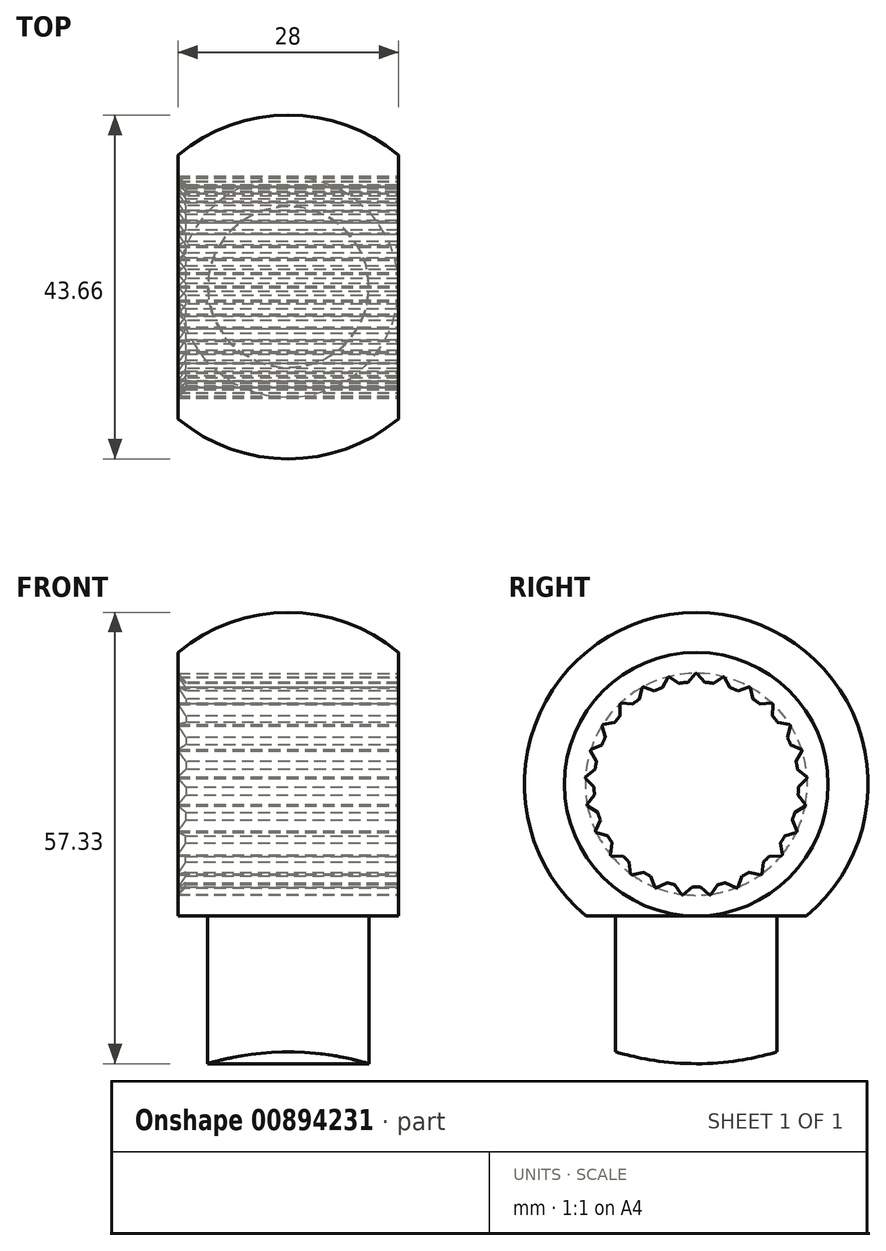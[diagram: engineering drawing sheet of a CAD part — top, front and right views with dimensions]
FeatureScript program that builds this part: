
annotation { "Feature Type Name" : "Feature", "Feature Type Description" : "" }
export const myFeature = defineFeature(function(context is Context, id is Id, definition is map)
    precondition{}
    {
        {
            var Q0;
            Q0=qCreatedBy(makeId("Front.planeOp"),FACE);
            var sketch = newSketch(context, id + "F0", { "sketchPlane" : qUnion([Q0])});
            skLineSegment(sketch, "E0", {"start": v(1, 13) * mm, "end": v(28, 13) * mm});
            skLineSegment(sketch, "E1", {"start": v(1, 13) * mm, "end": v(0, 14.1) * mm});
            skLineSegment(sketch, "E2", {"start": v(0, 14.1) * mm, "end": v(0, 16.75) * mm});
            skArc(sketch, "E3", {"start": v(28, 16.75) * mm, "mid": v(14, 21.83) * mm, "end": v(0, 16.75) * mm});
            skLineSegment(sketch, "E4", {"start": v(28, 16.75) * mm, "end": v(28, 13) * mm});
            skLineSegment(sketch, "E5", {"start": v(0, 0) * mm, "end": v(28, 0) * mm, "construction": true});
            skSolve(sketch);
        }
        {
            var Q0;
            Q0=makeQuery(id+"F0.imprint","IMPRINT",FACE,{"disambiguationData":[TD([[makeQuery(id+"F0.imprint","IMPRINT",EDGE,{"derivedFrom":sQuery(id+"F0.wireOp",EDGE,"E0")}),1.0]])]});
            var Q1;
            Q1=sQuery(id+"F0.wireOp",EDGE,"E5");
            revolve(context, id + "F1", {"surfaceOperationType" : NewSurfaceOperationType.NEW, "entities" : qUnion([Q0]), "axis" : qUnion([Q1]), "revolveType" : RevolveType.FULL});
        }
        {
            var Q0;
            Q0=qCreatedBy(makeId("Top.planeOp"),FACE);
            var sketch = newSketch(context, id + "F2", { "sketchPlane" : qUnion([Q0])});
            skCircle(sketch, "E6", {"center": v(14, 0) * mm, "radius": 10.25 * mm});
            skCircle(sketch, "E7", {"center": v(14, 0) * mm, "radius": 14 * mm});
            skSolve(sketch);
        }
        {
            var Q0;
            Q0=makeQuery(id+"F2.imprint","IMPRINT",FACE,{"disambiguationData":[TD([[makeQuery(id+"F2.imprint","IMPRINT",EDGE,{"derivedFrom":sQuery(id+"F2.wireOp",EDGE,"E6")}),-1.0]])]});
            extrude(context, id + "F3", {"entities" : qUnion([Q0]), "operationType" : NewBodyOperationType.REMOVE, "oppositeDirection" : true, "depth" : 21 * mm, "offsetDistance" : 25 * mm, "hasSecondDirection" : true, "secondDirectionOppositeDirection" : true, "secondDirectionDepth" : 16.75 * mm});
        }
        {
            var Q0;
            Q0=makeQuery(id+"F3.boolean.opBoolean","COPY",FACE,{"derivedFrom":makeQuery(id+"F3.opExtrude","CAP_FACE",FACE,{"disambiguationData":[OSD([sQuery(id+"F2.wireOp",EDGE,"E6"),sQuery(id+"F2.wireOp",EDGE,"E7")])],"isStart":true})});
            var sketch = newSketch(context, id + "F4", { "sketchPlane" : qUnion([Q0])});
            skCircle(sketch, "E8.0", {"center": v(14, 0) * mm, "radius": 10.25 * mm});
            skSolve(sketch);
        }
        {
            var Q0;
            Q0=qSketchRegion(id+"F4",true);
            extrude(context, id + "F5", {"entities" : qUnion([Q0]), "operationType" : NewBodyOperationType.ADD, "depth" : 20 * mm, "offsetDistance" : 25 * mm});
        }
        {
            var Q0;
            Q0=makeQuery(id+"F1.opRevolve","SWEPT_FACE",FACE,{"disambiguationData":[OSD([sQuery(id+"F0.wireOp",EDGE,"E2")])]});
            var sketch = newSketch(context, id + "F6", { "sketchPlane" : qUnion([Q0])});
            skCircle(sketch, "E9", {"center": v(0, 0) * mm, "radius": 35.5 * mm});
            skCircle(sketch, "E10", {"center": v(0, 0) * mm, "radius": 40 * mm});
            skSolve(sketch);
        }
        {
            var Q0;
            Q0=makeQuery(id+"F6.imprint","IMPRINT",FACE,{"disambiguationData":[TD([[makeQuery(id+"F6.imprint","IMPRINT",EDGE,{"derivedFrom":sQuery(id+"F6.wireOp",EDGE,"E9")}),-1.0]])]});
            extrude(context, id + "F7", {"entities" : qUnion([Q0]), "operationType" : NewBodyOperationType.REMOVE, "endBound" : BoundingType.THROUGH_ALL, "oppositeDirection" : true, "depth" : 25 * mm, "offsetDistance" : 25 * mm});
        }
        {
            var Q0;
            Q0=makeQuery(id+"F1.opRevolve","SWEPT_FACE",FACE,{"disambiguationData":[OSD([sQuery(id+"F0.wireOp",EDGE,"E4")])]});
            var sketch = newSketch(context, id + "F8", { "sketchPlane" : qUnion([Q0])});
            skArc(sketch, "E11", {"start": v(1.63, 12.85) * mm, "mid": v(1.38, 12.88) * mm, "end": v(1.13, 12.9) * mm});
            skArc(sketch, "E12", {"start": v(0.1, 14.05) * mm, "mid": v(0.05, 14.05) * mm, "end": v(0, 14.05) * mm});
            skLineSegment(sketch, "E13", {"start": v(0.1, 14.05) * mm, "end": v(1.13, 12.9) * mm});
            skArc(sketch, "E14", {"start": v(-1.13, 12.9) * mm, "mid": v(-1.38, 12.88) * mm, "end": v(-1.63, 12.85) * mm});
            skArc(sketch, "E15", {"start": v(0, 14.05) * mm, "mid": v(-0.05, 14.05) * mm, "end": v(-0.1, 14.05) * mm});
            skLineSegment(sketch, "E16", {"start": v(-0.1, 14.05) * mm, "end": v(-1.13, 12.9) * mm});
            skArc(sketch, "E17", {"start": v(-1.63, 12.85) * mm, "mid": v(-1.88, 12.81) * mm, "end": v(-2.13, 12.78) * mm});
            skArc(sketch, "E18", {"start": v(-3.4, 13.63) * mm, "mid": v(-3.46, 13.62) * mm, "end": v(-3.5, 13.6) * mm});
            skLineSegment(sketch, "E19", {"start": v(-3.4, 13.63) * mm, "end": v(-2.13, 12.78) * mm});
            skArc(sketch, "E20", {"start": v(-4.31, 12.21) * mm, "mid": v(-4.55, 12.13) * mm, "end": v(-4.79, 12.04) * mm});
            skArc(sketch, "E21", {"start": v(-3.5, 13.6) * mm, "mid": v(-3.55, 13.6) * mm, "end": v(-3.6, 13.58) * mm});
            skLineSegment(sketch, "E22", {"start": v(-3.6, 13.58) * mm, "end": v(-4.31, 12.21) * mm});
            skArc(sketch, "E23", {"start": v(-4.79, 12.04) * mm, "mid": v(-5.02, 11.94) * mm, "end": v(-5.25, 11.84) * mm});
            skArc(sketch, "E24", {"start": v(-6.7, 12.35) * mm, "mid": v(-6.75, 12.33) * mm, "end": v(-6.8, 12.3) * mm});
            skLineSegment(sketch, "E25", {"start": v(-6.7, 12.35) * mm, "end": v(-5.25, 11.84) * mm});
            skArc(sketch, "E26", {"start": v(-7.23, 10.76) * mm, "mid": v(-7.44, 10.61) * mm, "end": v(-7.64, 10.47) * mm});
            skArc(sketch, "E27", {"start": v(-6.8, 12.3) * mm, "mid": v(-6.84, 12.28) * mm, "end": v(-6.88, 12.26) * mm});
            skLineSegment(sketch, "E28", {"start": v(-6.88, 12.26) * mm, "end": v(-7.23, 10.76) * mm});
            skArc(sketch, "E29", {"start": v(-7.64, 10.47) * mm, "mid": v(-7.84, 10.32) * mm, "end": v(-8.04, 10.16) * mm});
            skArc(sketch, "E30", {"start": v(-9.58, 10.3) * mm, "mid": v(-9.62, 10.26) * mm, "end": v(-9.65, 10.23) * mm});
            skLineSegment(sketch, "E31", {"start": v(-9.58, 10.3) * mm, "end": v(-8.04, 10.16) * mm});
            skArc(sketch, "E32", {"start": v(-9.69, 8.62) * mm, "mid": v(-9.85, 8.43) * mm, "end": v(-10.02, 8.24) * mm});
            skArc(sketch, "E33", {"start": v(-9.65, 10.23) * mm, "mid": v(-9.69, 10.2) * mm, "end": v(-9.72, 10.16) * mm});
            skLineSegment(sketch, "E34", {"start": v(-9.72, 10.16) * mm, "end": v(-9.69, 8.62) * mm});
            skArc(sketch, "E35", {"start": v(-10.02, 8.24) * mm, "mid": v(-10.18, 8.04) * mm, "end": v(-10.33, 7.84) * mm});
            skArc(sketch, "E36", {"start": v(-11.85, 7.59) * mm, "mid": v(-11.88, 7.55) * mm, "end": v(-11.9, 7.5) * mm});
            skLineSegment(sketch, "E37", {"start": v(-11.85, 7.59) * mm, "end": v(-10.33, 7.84) * mm});
            skArc(sketch, "E38", {"start": v(-11.54, 5.94) * mm, "mid": v(-11.65, 5.71) * mm, "end": v(-11.76, 5.49) * mm});
            skArc(sketch, "E39", {"start": v(-11.9, 7.5) * mm, "mid": v(-11.93, 7.46) * mm, "end": v(-11.96, 7.42) * mm});
            skLineSegment(sketch, "E40", {"start": v(-11.96, 7.42) * mm, "end": v(-11.54, 5.94) * mm});
            skArc(sketch, "E41", {"start": v(-11.76, 5.49) * mm, "mid": v(-11.87, 5.26) * mm, "end": v(-11.97, 5.03) * mm});
            skArc(sketch, "E42", {"start": v(-13.38, 4.4) * mm, "mid": v(-13.4, 4.36) * mm, "end": v(-13.4, 4.3) * mm});
            skLineSegment(sketch, "E43", {"start": v(-13.38, 4.4) * mm, "end": v(-11.97, 5.03) * mm});
            skArc(sketch, "E44", {"start": v(-12.67, 2.88) * mm, "mid": v(-12.72, 2.63) * mm, "end": v(-12.77, 2.39) * mm});
            skArc(sketch, "E45", {"start": v(-13.4, 4.3) * mm, "mid": v(-13.43, 4.26) * mm, "end": v(-13.44, 4.21) * mm});
            skLineSegment(sketch, "E46", {"start": v(-13.44, 4.21) * mm, "end": v(-12.67, 2.88) * mm});
            skArc(sketch, "E47", {"start": v(-12.77, 2.39) * mm, "mid": v(-12.81, 2.14) * mm, "end": v(-12.85, 1.89) * mm});
            skArc(sketch, "E48", {"start": v(-14.07, 0.94) * mm, "mid": v(-14.07, 0.89) * mm, "end": v(-14.07, 0.84) * mm});
            skLineSegment(sketch, "E49", {"start": v(-14.07, 0.94) * mm, "end": v(-12.85, 1.89) * mm});
            skArc(sketch, "E50", {"start": v(-13, -0.36) * mm, "mid": v(-12.99, -0.61) * mm, "end": v(-12.97, -0.87) * mm});
            skArc(sketch, "E51", {"start": v(-14.07, 0.84) * mm, "mid": v(-14.08, 0.79) * mm, "end": v(-14.08, 0.74) * mm});
            skLineSegment(sketch, "E52", {"start": v(-14.08, 0.74) * mm, "end": v(-13, -0.36) * mm});
            skArc(sketch, "E53", {"start": v(-12.97, -0.87) * mm, "mid": v(-12.96, -1.12) * mm, "end": v(-12.93, -1.37) * mm});
            skArc(sketch, "E54", {"start": v(-13.87, -2.6) * mm, "mid": v(-13.86, -2.64) * mm, "end": v(-13.85, -2.7) * mm});
            skLineSegment(sketch, "E55", {"start": v(-13.87, -2.6) * mm, "end": v(-12.93, -1.37) * mm});
            skArc(sketch, "E56", {"start": v(-12.51, -3.58) * mm, "mid": v(-12.44, -3.83) * mm, "end": v(-12.36, -4.07) * mm});
            skArc(sketch, "E57", {"start": v(-13.85, -2.7) * mm, "mid": v(-13.84, -2.74) * mm, "end": v(-13.83, -2.79) * mm});
            skLineSegment(sketch, "E58", {"start": v(-13.83, -2.79) * mm, "end": v(-12.51, -3.58) * mm});
            skArc(sketch, "E59", {"start": v(-12.36, -4.07) * mm, "mid": v(-12.28, -4.3) * mm, "end": v(-12.2, -4.54) * mm});
            skArc(sketch, "E60", {"start": v(-12.8, -5.96) * mm, "mid": v(-12.78, -6) * mm, "end": v(-12.76, -6.05) * mm});
            skLineSegment(sketch, "E61", {"start": v(-12.8, -5.96) * mm, "end": v(-12.2, -4.54) * mm});
            skArc(sketch, "E62", {"start": v(-11.24, -6.58) * mm, "mid": v(-11.1, -6.8) * mm, "end": v(-10.98, -7.02) * mm});
            skArc(sketch, "E63", {"start": v(-12.76, -6.05) * mm, "mid": v(-12.74, -6.1) * mm, "end": v(-12.72, -6.14) * mm});
            skLineSegment(sketch, "E64", {"start": v(-12.72, -6.14) * mm, "end": v(-11.24, -6.58) * mm});
            skArc(sketch, "E65", {"start": v(-10.98, -7.02) * mm, "mid": v(-10.84, -7.23) * mm, "end": v(-10.7, -7.44) * mm});
            skArc(sketch, "E66", {"start": v(-10.93, -8.96) * mm, "mid": v(-10.9, -9) * mm, "end": v(-10.86, -9.04) * mm});
            skLineSegment(sketch, "E67", {"start": v(-10.93, -8.96) * mm, "end": v(-10.7, -7.44) * mm});
            skArc(sketch, "E68", {"start": v(-9.26, -9.17) * mm, "mid": v(-9.08, -9.35) * mm, "end": v(-8.9, -9.53) * mm});
            skArc(sketch, "E69", {"start": v(-10.86, -9.04) * mm, "mid": v(-10.83, -9.08) * mm, "end": v(-10.8, -9.11) * mm});
            skLineSegment(sketch, "E70", {"start": v(-10.8, -9.11) * mm, "end": v(-9.26, -9.17) * mm});
            skArc(sketch, "E71", {"start": v(-8.9, -9.53) * mm, "mid": v(-8.71, -9.7) * mm, "end": v(-8.53, -9.86) * mm});
            skArc(sketch, "E72", {"start": v(-8.37, -11.4) * mm, "mid": v(-8.33, -11.43) * mm, "end": v(-8.29, -11.46) * mm});
            skLineSegment(sketch, "E73", {"start": v(-8.37, -11.4) * mm, "end": v(-8.53, -9.86) * mm});
            skArc(sketch, "E74", {"start": v(-6.7, -11.2) * mm, "mid": v(-6.48, -11.32) * mm, "end": v(-6.26, -11.44) * mm});
            skArc(sketch, "E75", {"start": v(-8.29, -11.46) * mm, "mid": v(-8.25, -11.49) * mm, "end": v(-8.2, -11.52) * mm});
            skLineSegment(sketch, "E76", {"start": v(-8.2, -11.52) * mm, "end": v(-6.7, -11.2) * mm});
            skArc(sketch, "E77", {"start": v(-6.26, -11.44) * mm, "mid": v(-6.04, -11.56) * mm, "end": v(-5.82, -11.68) * mm});
            skArc(sketch, "E78", {"start": v(-5.28, -13.12) * mm, "mid": v(-5.24, -13.14) * mm, "end": v(-5.2, -13.16) * mm});
            skLineSegment(sketch, "E79", {"start": v(-5.28, -13.12) * mm, "end": v(-5.82, -11.68) * mm});
            skArc(sketch, "E80", {"start": v(-3.72, -12.5) * mm, "mid": v(-3.48, -12.58) * mm, "end": v(-3.23, -12.64) * mm});
            skArc(sketch, "E81", {"start": v(-5.2, -13.16) * mm, "mid": v(-5.14, -13.18) * mm, "end": v(-5.1, -13.2) * mm});
            skLineSegment(sketch, "E82", {"start": v(-5.1, -13.2) * mm, "end": v(-3.72, -12.5) * mm});
            skArc(sketch, "E83", {"start": v(-3.23, -12.64) * mm, "mid": v(-2.99, -12.7) * mm, "end": v(-2.74, -12.76) * mm});
            skArc(sketch, "E84", {"start": v(-1.87, -14.03) * mm, "mid": v(-1.82, -14.03) * mm, "end": v(-1.77, -14.04) * mm});
            skLineSegment(sketch, "E85", {"start": v(-1.87, -14.03) * mm, "end": v(-2.74, -12.76) * mm});
            skArc(sketch, "E86", {"start": v(-0.5, -13.04) * mm, "mid": v(-0.25, -13.05) * mm, "end": v(0, -13.05) * mm});
            skArc(sketch, "E87", {"start": v(-1.77, -14.04) * mm, "mid": v(-1.72, -14.04) * mm, "end": v(-1.67, -14.05) * mm});
            skLineSegment(sketch, "E88", {"start": v(-1.67, -14.05) * mm, "end": v(-0.5, -13.04) * mm});
            skArc(sketch, "E89", {"start": v(0, -13.05) * mm, "mid": v(0.25, -13.05) * mm, "end": v(0.5, -13.04) * mm});
            skArc(sketch, "E90", {"start": v(1.67, -14.05) * mm, "mid": v(1.72, -14.04) * mm, "end": v(1.77, -14.04) * mm});
            skLineSegment(sketch, "E91", {"start": v(1.67, -14.05) * mm, "end": v(0.5, -13.04) * mm});
            skArc(sketch, "E92", {"start": v(2.74, -12.76) * mm, "mid": v(2.99, -12.7) * mm, "end": v(3.23, -12.64) * mm});
            skArc(sketch, "E93", {"start": v(1.77, -14.04) * mm, "mid": v(1.82, -14.03) * mm, "end": v(1.87, -14.03) * mm});
            skLineSegment(sketch, "E94", {"start": v(1.87, -14.03) * mm, "end": v(2.74, -12.76) * mm});
            skArc(sketch, "E95", {"start": v(3.23, -12.64) * mm, "mid": v(3.48, -12.58) * mm, "end": v(3.72, -12.5) * mm});
            skArc(sketch, "E96", {"start": v(5.1, -13.2) * mm, "mid": v(5.14, -13.18) * mm, "end": v(5.2, -13.16) * mm});
            skLineSegment(sketch, "E97", {"start": v(5.1, -13.2) * mm, "end": v(3.72, -12.5) * mm});
            skArc(sketch, "E98", {"start": v(5.82, -11.68) * mm, "mid": v(6.04, -11.56) * mm, "end": v(6.26, -11.44) * mm});
            skArc(sketch, "E99", {"start": v(5.2, -13.16) * mm, "mid": v(5.24, -13.14) * mm, "end": v(5.28, -13.12) * mm});
            skLineSegment(sketch, "E100", {"start": v(5.28, -13.12) * mm, "end": v(5.82, -11.68) * mm});
            skArc(sketch, "E101", {"start": v(6.26, -11.44) * mm, "mid": v(6.48, -11.32) * mm, "end": v(6.7, -11.2) * mm});
            skArc(sketch, "E102", {"start": v(8.2, -11.52) * mm, "mid": v(8.25, -11.49) * mm, "end": v(8.29, -11.46) * mm});
            skLineSegment(sketch, "E103", {"start": v(8.2, -11.52) * mm, "end": v(6.7, -11.2) * mm});
            skArc(sketch, "E104", {"start": v(8.53, -9.86) * mm, "mid": v(8.71, -9.7) * mm, "end": v(8.9, -9.53) * mm});
            skArc(sketch, "E105", {"start": v(8.29, -11.46) * mm, "mid": v(8.33, -11.43) * mm, "end": v(8.37, -11.4) * mm});
            skLineSegment(sketch, "E106", {"start": v(8.37, -11.4) * mm, "end": v(8.53, -9.86) * mm});
            skArc(sketch, "E107", {"start": v(8.9, -9.53) * mm, "mid": v(9.08, -9.35) * mm, "end": v(9.26, -9.17) * mm});
            skArc(sketch, "E108", {"start": v(10.8, -9.11) * mm, "mid": v(10.83, -9.08) * mm, "end": v(10.86, -9.04) * mm});
            skLineSegment(sketch, "E109", {"start": v(10.8, -9.11) * mm, "end": v(9.26, -9.17) * mm});
            skArc(sketch, "E110", {"start": v(10.7, -7.44) * mm, "mid": v(10.84, -7.23) * mm, "end": v(10.98, -7.02) * mm});
            skArc(sketch, "E111", {"start": v(10.86, -9.04) * mm, "mid": v(10.9, -9) * mm, "end": v(10.93, -8.96) * mm});
            skLineSegment(sketch, "E112", {"start": v(10.93, -8.96) * mm, "end": v(10.7, -7.44) * mm});
            skArc(sketch, "E113", {"start": v(10.98, -7.02) * mm, "mid": v(11.1, -6.8) * mm, "end": v(11.24, -6.58) * mm});
            skArc(sketch, "E114", {"start": v(12.72, -6.14) * mm, "mid": v(12.74, -6.1) * mm, "end": v(12.76, -6.05) * mm});
            skLineSegment(sketch, "E115", {"start": v(12.72, -6.14) * mm, "end": v(11.24, -6.58) * mm});
            skArc(sketch, "E116", {"start": v(12.2, -4.54) * mm, "mid": v(12.28, -4.3) * mm, "end": v(12.36, -4.07) * mm});
            skArc(sketch, "E117", {"start": v(12.76, -6.05) * mm, "mid": v(12.78, -6) * mm, "end": v(12.8, -5.96) * mm});
            skLineSegment(sketch, "E118", {"start": v(12.8, -5.96) * mm, "end": v(12.2, -4.54) * mm});
            skArc(sketch, "E119", {"start": v(12.36, -4.07) * mm, "mid": v(12.44, -3.83) * mm, "end": v(12.51, -3.58) * mm});
            skArc(sketch, "E120", {"start": v(13.83, -2.79) * mm, "mid": v(13.84, -2.74) * mm, "end": v(13.85, -2.7) * mm});
            skLineSegment(sketch, "E121", {"start": v(13.83, -2.79) * mm, "end": v(12.51, -3.58) * mm});
            skArc(sketch, "E122", {"start": v(12.93, -1.37) * mm, "mid": v(12.96, -1.12) * mm, "end": v(12.97, -0.87) * mm});
            skArc(sketch, "E123", {"start": v(13.85, -2.7) * mm, "mid": v(13.86, -2.64) * mm, "end": v(13.87, -2.6) * mm});
            skLineSegment(sketch, "E124", {"start": v(13.87, -2.6) * mm, "end": v(12.93, -1.37) * mm});
            skArc(sketch, "E125", {"start": v(12.97, -0.87) * mm, "mid": v(12.99, -0.61) * mm, "end": v(13, -0.36) * mm});
            skArc(sketch, "E126", {"start": v(14.08, 0.74) * mm, "mid": v(14.08, 0.79) * mm, "end": v(14.07, 0.84) * mm});
            skLineSegment(sketch, "E127", {"start": v(14.08, 0.74) * mm, "end": v(13, -0.36) * mm});
            skArc(sketch, "E128", {"start": v(12.85, 1.89) * mm, "mid": v(12.81, 2.14) * mm, "end": v(12.77, 2.39) * mm});
            skArc(sketch, "E129", {"start": v(14.07, 0.84) * mm, "mid": v(14.07, 0.89) * mm, "end": v(14.07, 0.94) * mm});
            skLineSegment(sketch, "E130", {"start": v(14.07, 0.94) * mm, "end": v(12.85, 1.89) * mm});
            skArc(sketch, "E131", {"start": v(12.77, 2.39) * mm, "mid": v(12.72, 2.63) * mm, "end": v(12.67, 2.88) * mm});
            skArc(sketch, "E132", {"start": v(13.44, 4.21) * mm, "mid": v(13.43, 4.26) * mm, "end": v(13.4, 4.3) * mm});
            skLineSegment(sketch, "E133", {"start": v(13.44, 4.21) * mm, "end": v(12.67, 2.88) * mm});
            skArc(sketch, "E134", {"start": v(11.97, 5.03) * mm, "mid": v(11.87, 5.26) * mm, "end": v(11.76, 5.49) * mm});
            skArc(sketch, "E135", {"start": v(13.4, 4.3) * mm, "mid": v(13.4, 4.36) * mm, "end": v(13.38, 4.4) * mm});
            skLineSegment(sketch, "E136", {"start": v(13.38, 4.4) * mm, "end": v(11.97, 5.03) * mm});
            skArc(sketch, "E137", {"start": v(11.76, 5.49) * mm, "mid": v(11.65, 5.71) * mm, "end": v(11.54, 5.94) * mm});
            skArc(sketch, "E138", {"start": v(11.96, 7.42) * mm, "mid": v(11.93, 7.46) * mm, "end": v(11.9, 7.5) * mm});
            skLineSegment(sketch, "E139", {"start": v(11.96, 7.42) * mm, "end": v(11.54, 5.94) * mm});
            skArc(sketch, "E140", {"start": v(10.33, 7.84) * mm, "mid": v(10.18, 8.04) * mm, "end": v(10.02, 8.24) * mm});
            skArc(sketch, "E141", {"start": v(11.9, 7.5) * mm, "mid": v(11.88, 7.55) * mm, "end": v(11.85, 7.59) * mm});
            skLineSegment(sketch, "E142", {"start": v(11.85, 7.59) * mm, "end": v(10.33, 7.84) * mm});
            skArc(sketch, "E143", {"start": v(10.02, 8.24) * mm, "mid": v(9.85, 8.43) * mm, "end": v(9.69, 8.62) * mm});
            skArc(sketch, "E144", {"start": v(9.72, 10.16) * mm, "mid": v(9.69, 10.2) * mm, "end": v(9.65, 10.23) * mm});
            skLineSegment(sketch, "E145", {"start": v(9.72, 10.16) * mm, "end": v(9.69, 8.62) * mm});
            skArc(sketch, "E146", {"start": v(8.04, 10.16) * mm, "mid": v(7.84, 10.32) * mm, "end": v(7.64, 10.47) * mm});
            skArc(sketch, "E147", {"start": v(9.65, 10.23) * mm, "mid": v(9.62, 10.26) * mm, "end": v(9.58, 10.3) * mm});
            skLineSegment(sketch, "E148", {"start": v(9.58, 10.3) * mm, "end": v(8.04, 10.16) * mm});
            skArc(sketch, "E149", {"start": v(7.64, 10.47) * mm, "mid": v(7.44, 10.61) * mm, "end": v(7.23, 10.76) * mm});
            skArc(sketch, "E150", {"start": v(6.88, 12.26) * mm, "mid": v(6.84, 12.28) * mm, "end": v(6.8, 12.3) * mm});
            skLineSegment(sketch, "E151", {"start": v(6.88, 12.26) * mm, "end": v(7.23, 10.76) * mm});
            skArc(sketch, "E152", {"start": v(5.25, 11.84) * mm, "mid": v(5.02, 11.94) * mm, "end": v(4.79, 12.04) * mm});
            skArc(sketch, "E153", {"start": v(6.8, 12.3) * mm, "mid": v(6.75, 12.33) * mm, "end": v(6.7, 12.35) * mm});
            skLineSegment(sketch, "E154", {"start": v(6.7, 12.35) * mm, "end": v(5.25, 11.84) * mm});
            skArc(sketch, "E155", {"start": v(4.79, 12.04) * mm, "mid": v(4.55, 12.13) * mm, "end": v(4.31, 12.21) * mm});
            skArc(sketch, "E156", {"start": v(3.6, 13.58) * mm, "mid": v(3.55, 13.6) * mm, "end": v(3.5, 13.6) * mm});
            skLineSegment(sketch, "E157", {"start": v(3.6, 13.58) * mm, "end": v(4.31, 12.21) * mm});
            skArc(sketch, "E158", {"start": v(2.13, 12.78) * mm, "mid": v(1.88, 12.81) * mm, "end": v(1.63, 12.85) * mm});
            skArc(sketch, "E159", {"start": v(3.5, 13.6) * mm, "mid": v(3.46, 13.62) * mm, "end": v(3.4, 13.63) * mm});
            skLineSegment(sketch, "E160", {"start": v(3.4, 13.63) * mm, "end": v(2.13, 12.78) * mm});
            skCircle(sketch, "E161", {"center": v(0, -0.05) * mm, "radius": 12.03 * mm});
            skSolve(sketch);
        }
        {
            var Q0;
            Q0=qSketchRegion(id+"F8",true);
            extrude(context, id + "F9", {"entities" : qUnion([Q0]), "operationType" : NewBodyOperationType.REMOVE, "endBound" : BoundingType.THROUGH_ALL, "oppositeDirection" : true, "depth" : 25 * mm, "offsetDistance" : 25 * mm});
        }
    });
